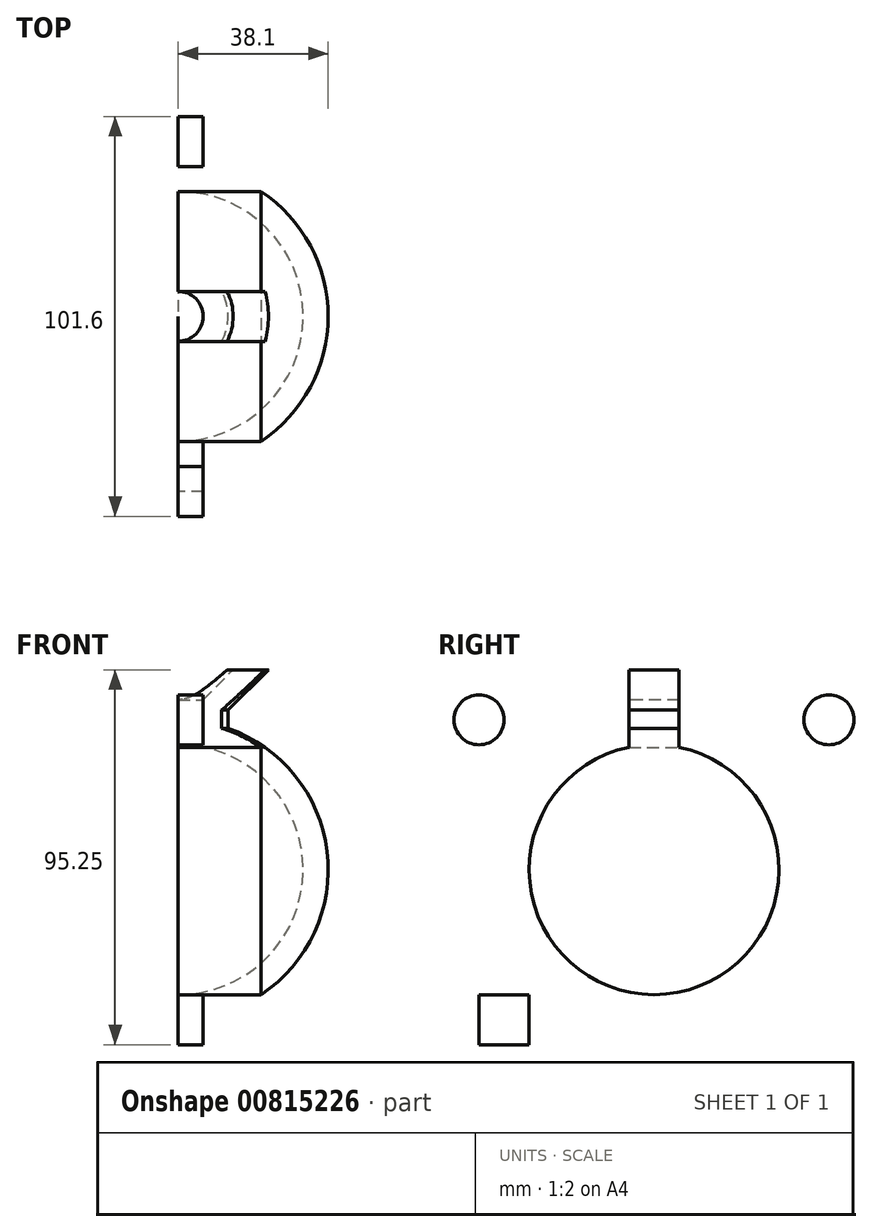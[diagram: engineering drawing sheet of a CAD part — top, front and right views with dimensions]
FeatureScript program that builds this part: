
annotation { "Feature Type Name" : "Feature", "Feature Type Description" : "" }
export const myFeature = defineFeature(function(context is Context, id is Id, definition is map)
    precondition{}
    {
        {
            var Q0;
            Q0=qCreatedBy(makeId("Right.planeOp"),FACE);
            var sketch = newSketch(context, id + "F0", { "sketchPlane" : qUnion([Q0])});
            skCircle(sketch, "E0", {"center": v(0, 0) * mm, "radius": 31.75 * mm});
            skLineSegment(sketch, "E1", {"start": v(0, -31.75) * mm, "end": v(0, -57.15) * mm});
            skLineSegment(sketch, "E2", {"start": v(0, -57.15) * mm, "end": v(57.15, -57.15) * mm});
            skLineSegment(sketch, "E3", {"start": v(57.15, -57.15) * mm, "end": v(57.15, 50.8) * mm});
            skLineSegment(sketch, "E4", {"start": v(57.15, 50.8) * mm, "end": v(6.35, 50.8) * mm});
            skLineSegment(sketch, "E5", {"start": v(6.35, 50.8) * mm, "end": v(6.35, 31.1) * mm});
            skSolve(sketch);
        }
        {
            var Q0;
            {var subQ0=sQuery(id+"F0.wireOp",EDGE,"E1");Q0=makeQuery(id+"F0.imprint","IMPRINT",FACE,{"disambiguationData":[TD([[makeQuery(id+"F0.imprint","IMPRINT",EDGE,{"derivedFrom":subQ0}),1.0]])]});}
            var Q1;
            Q1=sQuery(id+"F0.wireOp",EDGE,"E1");
            revolve(context, id + "F1", {"surfaceOperationType" : NewSurfaceOperationType.NEW, "entities" : qUnion([Q0]), "axis" : qUnion([Q1]), "revolveType" : RevolveType.ONE_DIRECTION, "angle" : 180 * degree});
        }
        {
            var Q0;
            Q0=makeQuery(id+"F1.opRevolve","CAP_FACE",FACE,{"disambiguationData":[OSD([sQuery(id+"F0.wireOp",EDGE,"E0"),sQuery(id+"F0.wireOp",EDGE,"E1"),sQuery(id+"F0.wireOp",EDGE,"E2"),sQuery(id+"F0.wireOp",EDGE,"E3"),sQuery(id+"F0.wireOp",EDGE,"E4"),sQuery(id+"F0.wireOp",EDGE,"E5")])],"isStart":false});
            var sketch = newSketch(context, id + "F2", { "sketchPlane" : qUnion([Q0])});
            skCircle(sketch, "E6", {"center": v(-44.45, 38.1) * mm, "radius": 6.35 * mm});
            skLineSegment(sketch, "E7.bottom", {"start": v(31.75, -31.75) * mm, "end": v(44.45, -31.75) * mm});
            skLineSegment(sketch, "E7.top", {"start": v(31.75, -44.45) * mm, "end": v(44.45, -44.45) * mm});
            skLineSegment(sketch, "E7.left", {"start": v(31.75, -31.75) * mm, "end": v(31.75, -44.45) * mm});
            skLineSegment(sketch, "E7.right", {"start": v(44.45, -31.75) * mm, "end": v(44.45, -44.45) * mm});
            skCircle(sketch, "E8.MirrorC", {"center": v(44.45, 38.1) * mm, "radius": 6.35 * mm});
            skLineSegment(sketch, "E9.MirrorCS", {"start": v(-31.75, -44.45) * mm, "end": v(-44.45, -44.45) * mm});
            skLineSegment(sketch, "E10.MirrorCS", {"start": v(-31.75, -31.75) * mm, "end": v(-31.75, -44.45) * mm});
            skLineSegment(sketch, "E11.MirrorCS", {"start": v(-44.45, -31.75) * mm, "end": v(-44.45, -44.45) * mm});
            skLineSegment(sketch, "E12.MirrorCS", {"start": v(-31.75, -31.75) * mm, "end": v(-44.45, -31.75) * mm});
            skSolve(sketch);
        }
        {
            var Q0;
            Q0=makeQuery(id+"F1.opRevolve","SWEPT_EDGE",EDGE,{"disambiguationData":[OSD([sQuery(id+"F0.wireOp",EDGE,"E4"),sQuery(id+"F0.wireOp",EDGE,"E5")])]});
            chamfer(context, id + "F3", {"entities" : qUnion([Q0]), "width" : 7.62 * mm, "tangentPropagation" : true});
        }
        {
            var Q0;
            Q0=makeQuery(id+"F1.opRevolve","SWEPT_FACE",FACE,{"disambiguationData":[OSD([sQuery(id+"F0.wireOp",EDGE,"E4")])]});
            var Q1;
            Q1=makeQuery(id+"F1.opRevolve","SWEPT_FACE",FACE,{"disambiguationData":[OSD([sQuery(id+"F0.wireOp",EDGE,"E3")])]});
            var Q2;
            Q2=makeQuery(id+"F1.opRevolve","SWEPT_FACE",FACE,{"disambiguationData":[OSD([sQuery(id+"F0.wireOp",EDGE,"E2")])]});
            shell(context, id + "F4", {"entities" : qUnion([Q0, Q1, Q2]), "thickness" : 6.35 * mm});
        }
        {
            var Q0;
            {var subQ0=sQuery(id+"F0.wireOp",EDGE,"E0");var subQ1=makeQuery(id+"F0.imprint","INTERSECT",VERTEX,{"derivedFrom":[subQ0,sQuery(id+"F0.wireOp",EDGE,"E1")]});Q0=makeQuery(id+"F0.imprint","IMPRINT",FACE,{"disambiguationData":[TD([[makeQuery(id+"F0.imprint","IMPRINT",EDGE,{"disambiguationData":[TD([[subQ1,1.0]])],"derivedFrom":subQ0}),1.0]])]});}
            var sketch = newSketch(context, id + "F5", { "sketchPlane" : qUnion([Q0])});
            skArc(sketch, "E13", {"start": v(24.87, 36.84) * mm, "mid": v(22.18, 38.52) * mm, "end": v(19.37, 40) * mm});
            skCircle(sketch, "E14", {"center": v(44.45, 0) * mm, "radius": 3.18 * mm});
            skCircle(sketch, "E15.1.0", {"center": v(22.12, 38.43) * mm, "radius": 3.18 * mm});
            skCircle(sketch, "E15.2.0", {"center": v(-22.32, 38.3) * mm, "radius": 3.18 * mm});
            skCircle(sketch, "E15.3.0", {"center": v(-44.44, -0.24) * mm, "radius": 3.18 * mm});
            skCircle(sketch, "E15.4.0", {"center": v(-22.11, -38.67) * mm, "radius": 3.18 * mm});
            skCircle(sketch, "E15.5.0", {"center": v(22.33, -38.55) * mm, "radius": 3.18 * mm});
            skPoint(sketch, "E15.center", {"position": v(0, -0.12) * mm});
            skArc(sketch, "E16.trimOffspring", {"start": v(-19.58, 39.9) * mm, "mid": v(-22.38, 38.4) * mm, "end": v(-25.07, 36.7) * mm});
            skArc(sketch, "E17.trimOffspring", {"start": v(-44.35, 2.93) * mm, "mid": v(-44.45, -0.24) * mm, "end": v(-44.32, -3.42) * mm});
            skArc(sketch, "E18.trimOffspring", {"start": v(-24.76, -36.92) * mm, "mid": v(-22.06, -38.59) * mm, "end": v(-19.26, -40.06) * mm});
            skArc(sketch, "E19.trimOffspring", {"start": v(19.48, -39.95) * mm, "mid": v(22.28, -38.46) * mm, "end": v(24.97, -36.78) * mm});
            skArc(sketch, "E20.trimOffspring", {"start": v(44.34, -3.17) * mm, "mid": v(44.45, 0) * mm, "end": v(44.34, 3.17) * mm});
            skSolve(sketch);
        }
        {
            var Q0;
            Q0 = qSketchRegion(id + "F5", true);
            extrude(context, id + "F6", {"entities" : qUnion([Q0]), "operationType" : NewBodyOperationType.REMOVE, "oppositeDirection" : true, "depth" : -12.7 * mm, "offsetDistance" : 25.4 * mm});
        }
        {
            var Q0;
            Q0=makeQuery(id+"F2.imprint","IMPRINT",FACE,{"disambiguationData":[TD([[makeQuery(id+"F2.imprint","IMPRINT",EDGE,{"derivedFrom":sQuery(id+"F2.wireOp",EDGE,"E8.MirrorC")}),-1.0]])]});
            var Q1;
            Q1=makeQuery(id+"F2.imprint","IMPRINT",FACE,{"disambiguationData":[TD([[makeQuery(id+"F2.imprint","IMPRINT",EDGE,{"derivedFrom":sQuery(id+"F2.wireOp",EDGE,"E9.MirrorCS")}),-1.0]])]});
            extrude(context, id + "F7", {"entities" : qUnion([Q0, Q1]), "operationType" : NewBodyOperationType.REMOVE, "oppositeDirection" : true, "depth" : 25.4 * mm, "offsetDistance" : 25.4 * mm});
        }
    });
